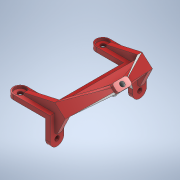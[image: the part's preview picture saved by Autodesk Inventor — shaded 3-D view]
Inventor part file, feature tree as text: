
AUTODESK INVENTOR PART (.ipt)
format: ipt  version: 2022 (Build 260153000, 153)  size: 563,200 bytes
history: native  units: mm
features: sketch x15, extrude x12, fillet x4, plane x3, hole x3, other x2, mirror x1, loft x1
ambient origin geometry x8: Origin, YZ Plane, XZ Plane, XY Plane, X Axis, Y Axis, Z Axis, Center Point
bodies: Body1 (feature_tree)
feature tree (41):
  extrude  "Extrusion6"  Depth=4.0mm
  plane  "Work Plane1"
  extrude  "Extrusion7"  Depth=2.0mm
  extrude  "Extrusion8"  Depth=28.504mm
  extrude  "Extrusion11"  Depth=6.362mm
  extrude  "Extrusion13"  Depth=24.240684mm
  hole  "Hole1"  [1 undecoded]
  plane  "Work Plane3"
  extrude  "Extrusion14"  Depth=6.5mm TaperAngle=0.0deg
  extrude  "Extrusion15"  Depth=2.0mm
  hole  "Hole2"  [1 undecoded]
  extrude  "Extrusion16"  Depth=1.0mm
  extrude  "Extrusion17"  Depth=1.0mm
  mirror  "Mirror1"
  extrude  "Extrusion18"  Depth=1.0mm
  loft  "Loft2"
  extrude  "Extrusion19"  Depth=10.0mm
  extrude  "Extrusion20"  Depth=4.0mm TaperAngle=0.0deg
  hole  "Hole3"  [1 undecoded]
  fillet  "Fillet1"  Radius=1.0mm
  fillet  "Fillet2"  Radius=2.0mm
  fillet  "Fillet3"  Radius=2.0mm
  fillet  "Fillet4"  Radius=1.0mm
  sketch  "Sketch7"  dims[d36=4.0mm d37=4.0mm]
  sketch  "Sketch9"  dims[d38=2.0mm d39=2.0mm]
  sketch  "Sketch10"  dims[d43=42.0mm d44=0.0mm d45=28.504mm]
  sketch  "Sketch14"  dims[d46=12.753mm d47=6.362mm]
  sketch  "Sketch16"  dims[d48=7.0mm d49=24.240684mm]
  sketch  "Sketch17"  dims[d50=1.5mm d51=90.0deg]
  sketch  "Sketch18"  dims[d52=3.5mm d53=6.5mm d54=0.0mm]
  sketch  "Sketch19"  dims[d55=2.0mm d56=2.0mm]
  sketch  "Sketch20"  dims[d57=2.0mm d58=2.0mm]
  sketch  "Sketch21"  dims[d59=1.0mm d60=1.0mm]
  sketch  "Sketch22"  dims[d61=1.0mm d62=1.0mm]
  plane  "Work Plane4"
  sketch  "Sketch23"  dims[d63=1.0mm d64=1.0mm]
  other  "Edges3"
  other  "Edges4"
  sketch  "Sketch24"  dims[d65=1.0mm d66=1.0mm]
  sketch  "Sketch27"  dims[d67=6.5mm d68=0.0mm d82=10.0mm]
  sketch  "Sketch28"  dims[d85=16.0mm d86=6.0mm d87=0.0mm d92=6.0mm d93=0.0mm d94=2.0mm d95=6.0mm d96=5.0mm d97=1.0mm d98=90.0deg d99=8.0mm d100=20.594885mm d101=1.0mm d102=2.0mm d103=0.0mm d104=2.0mm d105=0.0mm d106=2.0mm d107=6.0mm d108=5.0mm d109=1.0mm d110=90.0deg d111=8.0mm d112=20.594885mm d113=1.0mm d115=2.0mm d116=0.0mm d117=2.0mm d118=0.0mm d119=1.0mm d120=1.0mm d121=4.0mm d122=0.0mm d123=0.0mm d124=90.0deg d125=0.0mm d126=90.0deg d127=3.0mm d129=2.0mm d130=17.0mm d131=40.0mm d133=5.0mm d134=40.0mm d136=5.0mm d139=4.0mm d140=0.0mm d144=1.75mm d145=3.25mm d146=3.5mm d147=7.0mm d148=0.0mm d149=2.0mm d150=6.0mm d151=4.0mm d152=2.0mm d153=90.0deg d154=5.0mm d155=20.594885mm d156=3.0mm d157=2.0mm d158=1.0mm d159=4.0mm]
note: 3 required parameter values undecoded (feature->parameter linkage not recoverable at this tier; creation-order binding heuristic only, values carry confidence <= 0.55)
